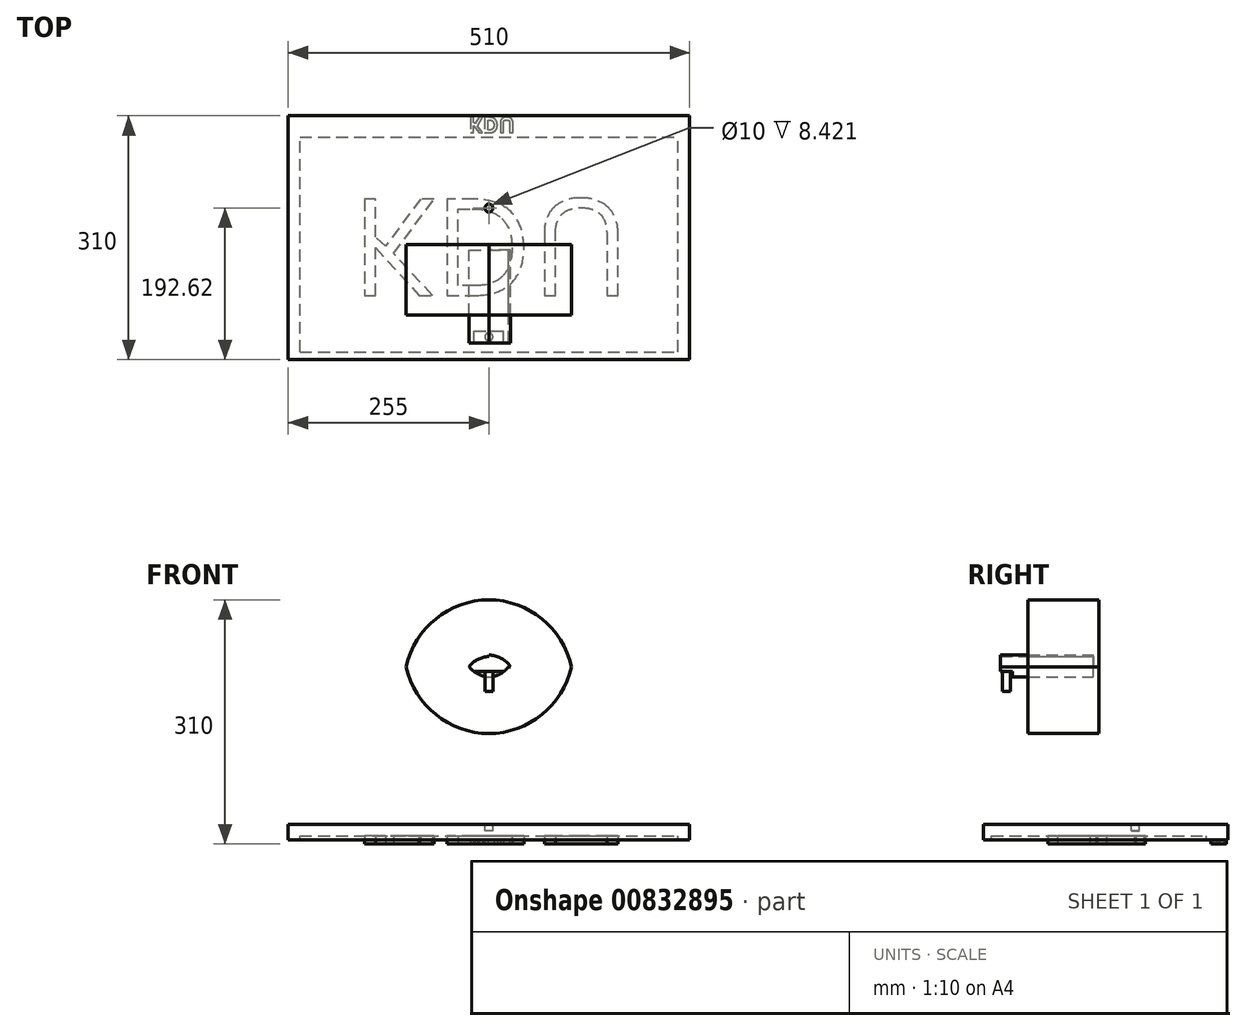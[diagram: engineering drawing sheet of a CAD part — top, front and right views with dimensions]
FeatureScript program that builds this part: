
annotation { "Feature Type Name" : "Feature", "Feature Type Description" : "" }
export const myFeature = defineFeature(function(context is Context, id is Id, definition is map)
    precondition{}
    {
        {
            var Q0;
            Q0=qCreatedBy(makeId("Front.planeOp"),FACE);
            var sketch = newSketch(context, id + "F0", { "sketchPlane" : qUnion([Q0])});
            skLineSegment(sketch, "E0", {"start": v(-105, 0) * mm, "end": v(105, 0) * mm});
            skLineSegment(sketch, "E1", {"start": v(0, 0) * mm, "end": v(0, 85) * mm});
            skArc(sketch, "E2", {"start": v(0, 85) * mm, "mid": v(-67.3, 60.79) * mm, "end": v(-105, 0) * mm});
            skArc(sketch, "E3.MirrorCS", {"start": v(0, 85) * mm, "mid": v(67.3, 60.79) * mm, "end": v(105, 0) * mm});
            skArc(sketch, "E4.MirrorCS", {"start": v(0, -85) * mm, "mid": v(67.3, -60.79) * mm, "end": v(105, 0) * mm});
            skArc(sketch, "E5.MirrorCS", {"start": v(0, -85) * mm, "mid": v(-67.3, -60.79) * mm, "end": v(-105, 0) * mm});
            skSolve(sketch);
        }
        {
            var Q0;
            Q0 = qSketchRegion(id + "F0", true);
            extrude(context, id + "F1", {"entities" : qUnion([Q0]), "depth" : 7 * mm, "offsetDistance" : 25 * mm});
        }
        {
            var Q0;
            Q0=makeQuery(id+"F1.opExtrude","CAP_FACE",FACE,{"disambiguationData":[OSD([sQuery(id+"F0.wireOp",EDGE,"E2"),sQuery(id+"F0.wireOp",EDGE,"E3.MirrorCS"),sQuery(id+"F0.wireOp",EDGE,"E4.MirrorCS"),sQuery(id+"F0.wireOp",EDGE,"E5.MirrorCS")])],"isStart":false});
            var sketch = newSketch(context, id + "F2", { "sketchPlane" : qUnion([Q0])});
            skLineSegment(sketch, "E6", {"start": v(-27.5, 0) * mm, "end": v(27.5, 0) * mm});
            skLineSegment(sketch, "E7", {"start": v(0, 0) * mm, "end": v(0, 15) * mm});
            skArc(sketch, "E8", {"start": v(0, 15) * mm, "mid": v(-15.51, 10.73) * mm, "end": v(-27.5, 0) * mm});
            skArc(sketch, "E9.MirrorCS", {"start": v(0, 15) * mm, "mid": v(15.51, 10.73) * mm, "end": v(27.5, 0) * mm});
            skLineSegment(sketch, "E10.MirrorCS", {"start": v(27.5, 0) * mm, "end": v(-27.5, 0) * mm});
            skArc(sketch, "E11.MirrorCS", {"start": v(0, -15) * mm, "mid": v(15.51, -10.73) * mm, "end": v(27.5, 0) * mm});
            skArc(sketch, "E12.MirrorCS", {"start": v(0, -15) * mm, "mid": v(-15.51, -10.73) * mm, "end": v(-27.5, 0) * mm});
            skArc(sketch, "E13.0", {"start": v(0, -13) * mm, "mid": v(14.59, -8.96) * mm, "end": v(25.86, 1.14) * mm});
            skArc(sketch, "E13.1", {"start": v(0, -13) * mm, "mid": v(-13.96, -9.3) * mm, "end": v(-25.02, 0) * mm});
            skArc(sketch, "E13.2", {"start": v(0.07, 13) * mm, "mid": v(-13.93, 9.31) * mm, "end": v(-25.02, 0) * mm});
            skArc(sketch, "E14.0", {"start": v(-0.07, 13) * mm, "mid": v(14.56, 8.98) * mm, "end": v(25.86, -1.14) * mm});
            skSolve(sketch);
        }
        {
            var Q0;
            {var subQ0=sQuery(id+"F2.wireOp",EDGE,"E8");Q0=makeQuery(id+"F2.imprint","IMPRINT",FACE,{"disambiguationData":[TD([[makeQuery(id+"F2.imprint","IMPRINT",EDGE,{"derivedFrom":subQ0}),1.0]])]});}
            var Q1;
            {var subQ0=sQuery(id+"F2.wireOp",EDGE,"E9.MirrorCS");Q1=makeQuery(id+"F2.imprint","IMPRINT",FACE,{"disambiguationData":[TD([[makeQuery(id+"F2.imprint","IMPRINT",EDGE,{"derivedFrom":subQ0}),-1.0]])]});}
            var Q2;
            {var subQ3=sQuery(id+"F2.wireOp",EDGE,"E11.MirrorCS");Q2=makeQuery(id+"F2.imprint","IMPRINT",FACE,{"disambiguationData":[TD([[makeQuery(id+"F2.imprint","IMPRINT",EDGE,{"derivedFrom":subQ3}),1.0]])]});}
            extrude(context, id + "F3", {"entities" : qUnion([Q0, Q1, Q2]), "operationType" : NewBodyOperationType.ADD, "depth" : 83 * mm, "offsetDistance" : 25 * mm});
        }
        {
            var Q0;
            Q0=qCreatedBy(makeId("Top.planeOp"),FACE);
            cPlane(context, id + "F4", {"entities" : qUnion([Q0]), "cplaneType" : CPlaneType.OFFSET, "offset" : 200 * mm, "oppositeDirection" : true, "width" : 150 * mm, "height" : 150 * mm});
        }
        {
            var Q0;
            Q0=qCreatedBy(id+"F4.planeOp",FACE);
            var sketch = newSketch(context, id + "F5", { "sketchPlane" : qUnion([Q0])});
            skLineSegment(sketch, "E15.bottom", {"start": v(-255, -146.5) * mm, "end": v(255, -146.5) * mm});
            skLineSegment(sketch, "E15.top", {"start": v(-255, 163.5) * mm, "end": v(255, 163.5) * mm});
            skLineSegment(sketch, "E15.left", {"start": v(-255, -146.5) * mm, "end": v(-255, 163.5) * mm});
            skLineSegment(sketch, "E15.right", {"start": v(255, -146.5) * mm, "end": v(255, 163.5) * mm});
            skPoint(sketch, "E15.middle", {"position": v(0, 0) * mm});
            skLineSegment(sketch, "E16.bottom", {"start": v(-240, -136.5) * mm, "end": v(240, -136.5) * mm});
            skLineSegment(sketch, "E16.top", {"start": v(-240, 136.5) * mm, "end": v(240, 136.5) * mm});
            skLineSegment(sketch, "E16.left", {"start": v(-240, -136.5) * mm, "end": v(-240, 136.5) * mm});
            skLineSegment(sketch, "E16.right", {"start": v(240, -136.5) * mm, "end": v(240, 136.5) * mm});
            skSolve(sketch);
        }
        {
            var Q0;
            Q0=makeQuery(id+"F5.imprint","IMPRINT",FACE,{"disambiguationData":[TD([[makeQuery(id+"F5.imprint","IMPRINT",EDGE,{"derivedFrom":sQuery(id+"F5.wireOp",EDGE,"E15.bottom")}),1.0]])]});
            extrude(context, id + "F6", {"entities" : qUnion([Q0]), "oppositeDirection" : true, "depth" : 20 * mm, "offsetDistance" : 25 * mm});
        }
        {
            var Q0;
            Q0=makeQuery(id+"F5.imprint","IMPRINT",FACE,{"disambiguationData":[TD([[makeQuery(id+"F5.imprint","IMPRINT",EDGE,{"derivedFrom":sQuery(id+"F5.wireOp",EDGE,"E16.bottom")}),1.0]])]});
            extrude(context, id + "F7", {"entities" : qUnion([Q0]), "operationType" : NewBodyOperationType.ADD, "oppositeDirection" : true, "depth" : 15 * mm, "offsetDistance" : 25 * mm});
        }
        {
            var Q0;
            Q0=makeQuery(id+"F6.opExtrude","CAP_FACE",FACE,{"disambiguationData":[OSD([sQuery(id+"F5.wireOp",EDGE,"E15.bottom"),sQuery(id+"F5.wireOp",EDGE,"E15.top"),sQuery(id+"F5.wireOp",EDGE,"E15.left"),sQuery(id+"F5.wireOp",EDGE,"E15.right"),sQuery(id+"F5.wireOp",EDGE,"E16.bottom"),sQuery(id+"F5.wireOp",EDGE,"E16.top"),sQuery(id+"F5.wireOp",EDGE,"E16.left"),sQuery(id+"F5.wireOp",EDGE,"E16.right")])],"isStart":false});
            cPlane(context, id + "F8", {"entities" : qUnion([Q0]), "cplaneType" : CPlaneType.OFFSET, "offset" : 5 * mm, "width" : 150 * mm, "height" : 150 * mm});
        }
        {
            var Q0;
            Q0=makeQuery(id+"F3.boolean.opBoolean","SPLIT",FACE,{"disambiguationData":[TD([makeQuery(id+"F3.opExtrude","SWEPT_FACE",FACE,{"disambiguationData":[OSD([sQuery(id+"F2.wireOp",EDGE,"E13.0")])]})])],"derivedFrom":makeQuery(id+"F1.opExtrude","CAP_FACE",FACE,{"disambiguationData":[OSD([sQuery(id+"F0.wireOp",EDGE,"E2"),sQuery(id+"F0.wireOp",EDGE,"E3.MirrorCS"),sQuery(id+"F0.wireOp",EDGE,"E4.MirrorCS"),sQuery(id+"F0.wireOp",EDGE,"E5.MirrorCS")])],"isStart":false})});
            extrude(context, id + "F9", {"entities" : qUnion([Q0]), "depth" : (83 + 20) * mm, "offsetDistance" : 25 * mm});
        }
        {
            var Q0;
            Q0=makeQuery(id+"F9.opExtrude","CAP_FACE",FACE,{"disambiguationData":[OSD([sQuery(id+"F0.wireOp",EDGE,"E2"),sQuery(id+"F0.wireOp",EDGE,"E3.MirrorCS"),sQuery(id+"F0.wireOp",EDGE,"E4.MirrorCS"),sQuery(id+"F0.wireOp",EDGE,"E5.MirrorCS")])],"isStart":false});
            var sketch = newSketch(context, id + "F10", { "sketchPlane" : qUnion([Q0])});
            skLineSegment(sketch, "E17", {"start": v(-18.74, -6.27) * mm, "end": v(18.74, -6.27) * mm});
            skSolve(sketch);
        }
        {
            var Q0;
            {var subQ2=sQuery(id+"F10.wireOp",EDGE,"E17");Q0=makeQuery(id+"F10.imprint","IMPRINT",FACE,{"disambiguationData":[TD([[makeQuery(id+"F10.imprint","IMPRINT",EDGE,{"derivedFrom":subQ2}),1.0]])]});}
            extrude(context, id + "F11", {"entities" : qUnion([Q0]), "operationType" : NewBodyOperationType.ADD, "depth" : 15 * mm, "offsetDistance" : 25 * mm});
        }
        {
            var Q0;
            Q0=makeQuery(id+"F11.opExtrude","SWEPT_FACE",FACE,{"disambiguationData":[OSD([sQuery(id+"F10.wireOp",EDGE,"E17")])]});
            var sketch = newSketch(context, id + "F12", { "sketchPlane" : qUnion([Q0])});
            skLineSegment(sketch, "E18", {"start": v(-18.74, 110) * mm, "end": v(0, 110) * mm});
            skLineSegment(sketch, "E19", {"start": v(0, 110) * mm, "end": v(0, 117.5) * mm});
            skPoint(sketch, "E19.endSnap0", {"position": v(0, 125) * mm});
            skCircle(sketch, "E20", {"center": v(0, 117.5) * mm, "radius": 5 * mm});
            skSolve(sketch);
        }
        {
            var Q0;
            Q0=makeQuery(id+"F12.imprint","IMPRINT",FACE,{"disambiguationData":[TD([[makeQuery(id+"F12.imprint","IMPRINT",EDGE,{"derivedFrom":sQuery(id+"F12.wireOp",EDGE,"E20")}),1.0]])]});
            extrude(context, id + "F13", {"entities" : qUnion([Q0]), "operationType" : NewBodyOperationType.ADD, "depth" : 25 * mm, "offsetDistance" : 25 * mm});
        }
        {
            var Q0;
            Q0=makeQuery(id+"F5.imprint","IMPRINT",FACE,{"disambiguationData":[TD([[makeQuery(id+"F5.imprint","IMPRINT",EDGE,{"derivedFrom":sQuery(id+"F5.wireOp",EDGE,"E15.bottom")}),1.0]])]});
            var sketch = newSketch(context, id + "F14", { "sketchPlane" : qUnion([Q0])});
            skLineSegment(sketch, "E21", {"start": v(0, 161.12) * mm, "end": v(0, 46.12) * mm});
            skCircle(sketch, "E22", {"center": v(0, 46.12) * mm, "radius": 5 * mm});
            skSolve(sketch);
        }
        {
            var Q0;
            Q0=makeQuery(id+"F14.imprint","IMPRINT",FACE,{"disambiguationData":[TD([[makeQuery(id+"F14.imprint","IMPRINT",EDGE,{"derivedFrom":sQuery(id+"F14.wireOp",EDGE,"E22")}),1.0]])]});
            var Q1;
            Q1=sQuery(id+"F14.wireOp",EDGE,"E22");
            extrude(context, id + "F15", {"entities" : qUnion([Q0]), "operationType" : NewBodyOperationType.REMOVE, "surfaceEntities" : qUnion([Q1]), "oppositeDirection" : true, "depth" : (15 - 6.58) * mm, "offsetDistance" : 25 * mm});
        }
        {
            var Q0;
            Q0=qCreatedBy(id+"F8.planeOp",FACE);
            var sketch = newSketch(context, id + "F16", { "sketchPlane" : qUnion([Q0])});
            skText(sketch, "E23", { "text": "KDU", "fontName": "OpenSans-Bold.ttf"});
            skText(sketch, "E24", { "text": "KDU", "fontName": "OpenSans-Regular.ttf"});
            const initialGuessF16  = {"E23": [-0.02596, -0.16141, 1, 0, 0.01959], "E24": [-0.175, -0.05744, 1, 0, 0.12324]};
            skSetInitialGuess(sketch, initialGuessF16);
            skSolve(sketch);
        }
        {
            var Q0;
            Q0 = qSketchRegion(id + "F16", true);
            extrude(context, id + "F17", {"entities" : qUnion([Q0]), "operationType" : NewBodyOperationType.ADD, "endBound" : BoundingType.UP_TO_NEXT, "oppositeDirection" : true, "depth" : 25 * mm, "offsetDistance" : 25 * mm});
        }
    });
